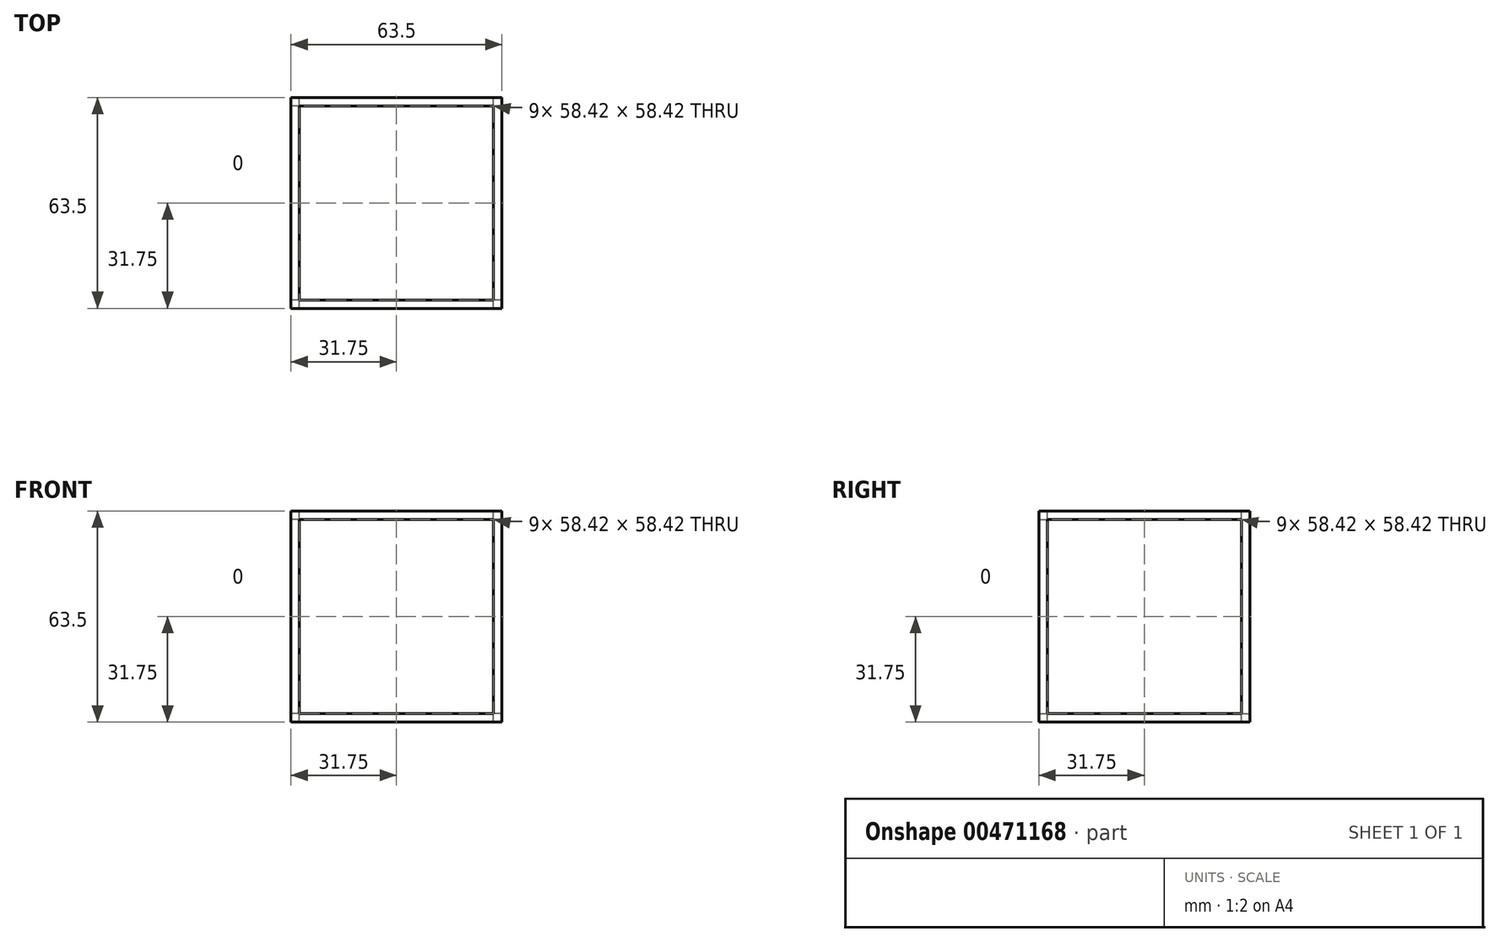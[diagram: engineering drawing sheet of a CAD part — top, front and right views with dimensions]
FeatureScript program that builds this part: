
annotation { "Feature Type Name" : "Feature", "Feature Type Description" : "" }
export const myFeature = defineFeature(function(context is Context, id is Id, definition is map)
    precondition{}
    {
        {
            var Q0;
            Q0=qCreatedBy(makeId("Top.planeOp"),FACE);
            var sketch = newSketch(context, id + "F0", { "sketchPlane" : qUnion([Q0])});
            skLineSegment(sketch, "E0.bottom", {"start": v(31.75, 31.75) * mm, "end": v(-31.75, 31.75) * mm});
            skLineSegment(sketch, "E0.top", {"start": v(31.75, -31.75) * mm, "end": v(-31.75, -31.75) * mm});
            skLineSegment(sketch, "E0.left", {"start": v(31.75, 31.75) * mm, "end": v(31.75, -31.75) * mm});
            skLineSegment(sketch, "E0.right", {"start": v(-31.75, 31.75) * mm, "end": v(-31.75, -31.75) * mm});
            skSolve(sketch);
        }
        {
            var Q0;
            Q0 = qSketchRegion(id + "F0", true);
            extrude(context, id + "F1", {"entities" : qUnion([Q0]), "endBound" : BoundingType.SYMMETRIC, "depth" : 63.5 * mm});
        }
        {
            var Q0;
            Q0=makeQuery(id+"F1.opExtrude","SWEPT_FACE",FACE,{"disambiguationData":[OSD([sQuery(id+"F0.wireOp",EDGE,"E0.right")])]});
            shell(context, id + "F2", {"entities" : qUnion([Q0]), "thickness" : 2.54 * mm});
        }
        {
            var Q0;
            Q0=makeQuery(id+"F2.opShell","OFFSET_FACE",FACE,{"disambiguationData":[OSD([sQuery(id+"F0.wireOp",EDGE,"E0.left")])]});
            extrude(context, id + "F3", {"entities" : qUnion([Q0]), "operationType" : NewBodyOperationType.REMOVE, "endBound" : BoundingType.THROUGH_ALL, "oppositeDirection" : true, "depth" : 25.4 * mm});
        }
        {
            var Q0;
            Q0=makeQuery(id+"F1.opExtrude","CAP_FACE",FACE,{"disambiguationData":[OSD([sQuery(id+"F0.wireOp",EDGE,"E0.bottom"),sQuery(id+"F0.wireOp",EDGE,"E0.top"),sQuery(id+"F0.wireOp",EDGE,"E0.left"),sQuery(id+"F0.wireOp",EDGE,"E0.right")])],"isStart":false});
            var sketch = newSketch(context, id + "F4", { "sketchPlane" : qUnion([Q0])});
            skLineSegment(sketch, "E1.bottom", {"start": v(29.2, 29.21) * mm, "end": v(-29.21, 29.2) * mm});
            skLineSegment(sketch, "E1.top", {"start": v(29.21, -29.2) * mm, "end": v(-29.21, -29.21) * mm});
            skLineSegment(sketch, "E1.left", {"start": v(29.2, 29.21) * mm, "end": v(29.21, -29.2) * mm});
            skLineSegment(sketch, "E1.right", {"start": v(-29.21, 29.2) * mm, "end": v(-29.21, -29.21) * mm});
            skSolve(sketch);
        }
        {
            var Q0;
            Q0 = qSketchRegion(id + "F4", true);
            extrude(context, id + "F5", {"entities" : qUnion([Q0]), "operationType" : NewBodyOperationType.REMOVE, "endBound" : BoundingType.THROUGH_ALL, "oppositeDirection" : true, "depth" : 25.4 * mm});
        }
        {
            var Q0;
            Q0=makeQuery(id+"F1.opExtrude","SWEPT_FACE",FACE,{"disambiguationData":[OSD([sQuery(id+"F0.wireOp",EDGE,"E0.bottom")])]});
            var sketch = newSketch(context, id + "F6", { "sketchPlane" : qUnion([Q0])});
            skLineSegment(sketch, "E2.bottom", {"start": v(29.21, 29.21) * mm, "end": v(-29.21, 29.2) * mm});
            skLineSegment(sketch, "E2.top", {"start": v(29.21, -29.2) * mm, "end": v(-29.2, -29.21) * mm});
            skLineSegment(sketch, "E2.left", {"start": v(29.21, 29.21) * mm, "end": v(29.21, -29.2) * mm});
            skLineSegment(sketch, "E2.right", {"start": v(-29.21, 29.2) * mm, "end": v(-29.2, -29.21) * mm});
            skSolve(sketch);
        }
        {
            var Q0;
            Q0 = qSketchRegion(id + "F6", true);
            extrude(context, id + "F7", {"entities" : qUnion([Q0]), "operationType" : NewBodyOperationType.REMOVE, "endBound" : BoundingType.THROUGH_ALL, "oppositeDirection" : true, "depth" : 25.4 * mm});
        }
    });
